# Revit family: Backless Units
name_source: partatom
category: Furniture
units: mm (PartAtom-declared; Revit-internal decimal feet)

## family parameters
Always vertical = Yes
Cut with Voids When Loaded = No
OmniClass Number = 23.40.20.00
OmniClass Title = General Furniture and Specialties
Room Calculation Point = No
Shared = No
Work Plane-Based = No

## types (16) — shared parameters
Default Elevation = 0' - 0"
Manufacturer = AIS Inc
Product = BACKLESS UNITS
URL = https://www.ais-inc.com

## per-type parameters (varying)
| type | Description |
| F-SBCR303030C | 30Wx30Dx18H Configurable LB Lounge Backless Unit Open Base (1-Cushion) |
| F-SBCR303630C | 36Wx30Dx18H Configurable LB Lounge Backless Unit Open Base (2-Cushion) |
| F-SBCR304230C | 42Wx30Dx18H Configurable LB Lounge Backless Unit Open Base (2-Cushion) |
| F-SBCR304830C | 48Wx30Dx18HConfigurable LB Lounge Backless Unit Open Base (2-Cushion) |
| F-SBCR305430C | 54Wx30Dx18H Configurable LB Lounge Backless Unit Open Base (2-Cushion) |
| F-SBCR306030C | 60Wx30Dx18H Configurable LB Lounge Backless Unit Open Base (2-Cushion) |
| F-SBCR306630C | 66Wx30Dx18H Configurable LB Lounge Backless Unit Open Base (3-Cushion) |
| F-SBCR307230C | 72Wx30Dx18H Configurable LB Lounge Backless Unit Open Base (3-Cushion) |
| F-SCCR303030C | 30Wx30Dx18H Configurable LB Lounge Backless Unit Solid Base (1-Cushion) |
| F-SCCR303630C | 36Wx30Dx18H Configurable LB Lounge Backless Unit Solid Base (2-Cushion) |
| F-SCCR304230C | 42Wx30Dx18H Configurable LB Lounge Backless Unit Solid Base (2-Cushion) |
| F-SCCR304830C | 48Wx30D18H Configurable LB Lounge Backless Unit Solid Base (2-Cushion) |
| F-SCCR305430C | 54Wx30Dx18H Configurable LB Lounge Backless Unit Solid Base (2-Cushion) |
| F-SCCR306030C | 60Wx30Dx18H Configurable LB Lounge Backless Unit Solid Base (2-Cushion) |
| F-SCCR306630C | 66Wx30Dx18H Configurable LB Lounge Backless Unit Solid Base (3-Cushion) |
| F-SCCR307230C | 72Wx30Dx18H Configurable LB Lounge Backless Unit Solid Base (3-Cushion) |

note: column(s) folded — value = type name in every type: Model

type visibility flags: 16 boolean params named "<type name>" — each type sets only its own to Yes (folded from table)

## geometry (parser evidence)
native form markers: Sweep x3
no freeform markers — native parametric forms only
